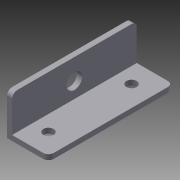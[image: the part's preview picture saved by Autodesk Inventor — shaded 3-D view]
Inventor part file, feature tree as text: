
AUTODESK INVENTOR PART (.ipt)
format: ipt  version: 2012 (Build 160160000, 160)  size: 107,008 bytes
history: native  units: in
note: dims shown in document units (in); Inventor stores cm internally (conversion verified against a paired STEP export)
features: extrude x3, sketch x3, fillet x1
ambient origin geometry x8: Origin, YZ Plane, XZ Plane, XY Plane, X Axis, Y Axis, Z Axis, Center Point
bodies: Solid1 (feature_tree)
feature tree (7):
  extrude  "Extrusion1"  Depth=0.125in
  fillet  "Fillet1"  Radius=1.0in
  extrude  "Extrusion2"  Depth=3.0in TaperAngle=0.0deg
  extrude  "Extrusion3"  Depth=0.375in
  sketch  "Sketch1"  dims[d0=0.125in d1=0.125in d2=1.0in]
  sketch  "Sketch2"  dims[d3=1.0in d4=3.0in d5=0.0in]
  sketch  "Sketch3"  dims[d6=0.125in d7=0.375in d8=4.0in d9=0.0in d10=0.5in d11=0.25in d12=0.25in d13=4.0in d14=0.0in]
